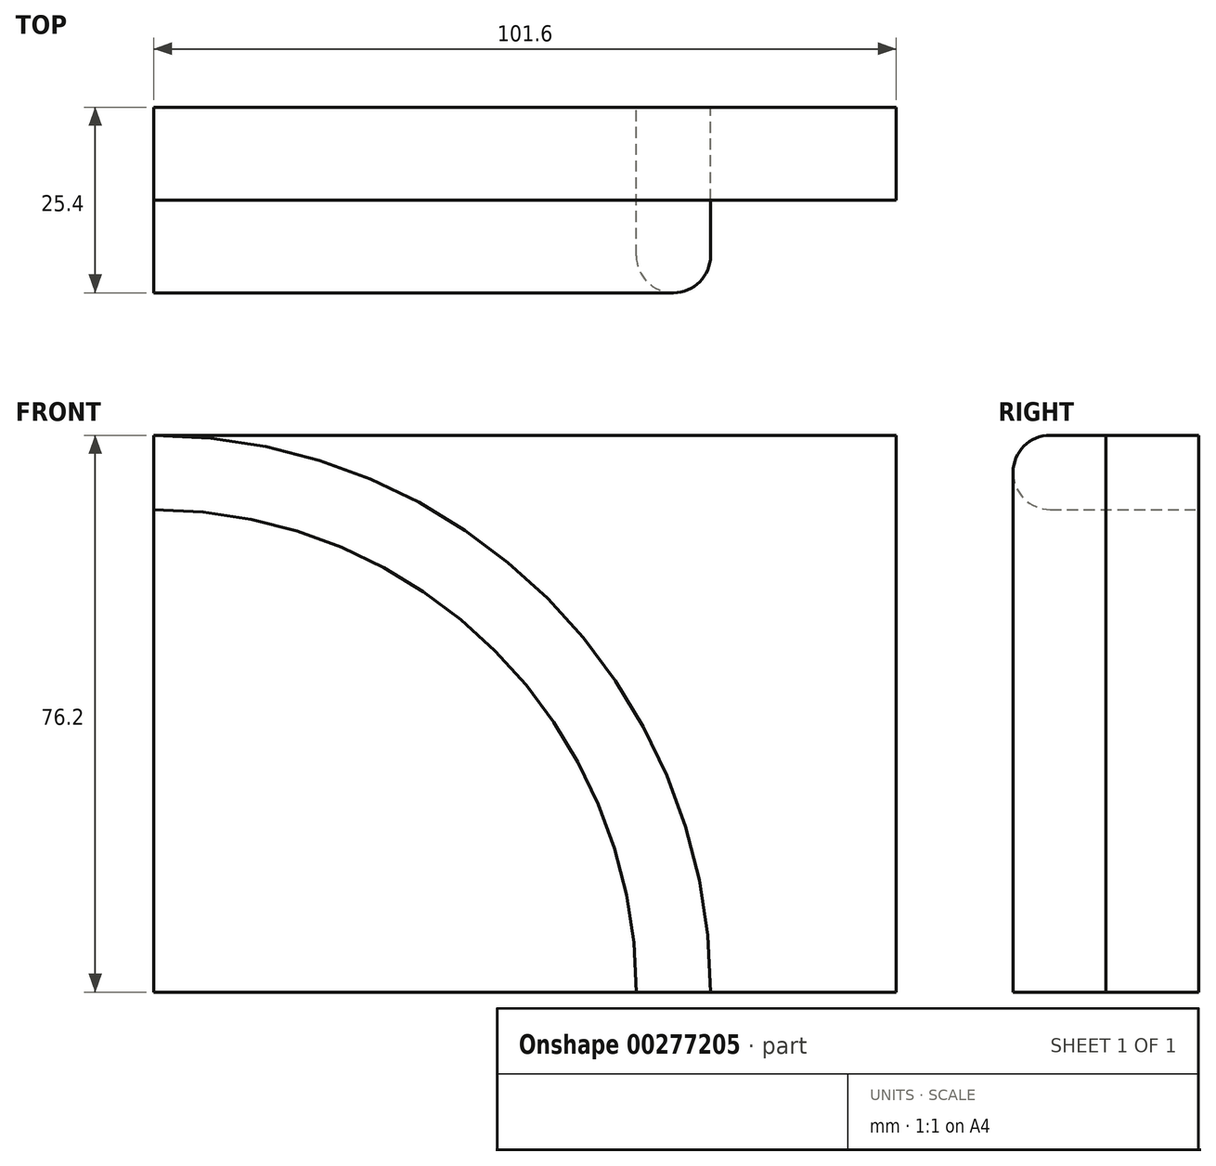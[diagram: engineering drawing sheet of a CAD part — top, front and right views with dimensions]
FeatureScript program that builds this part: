
annotation { "Feature Type Name" : "Feature", "Feature Type Description" : "" }
export const myFeature = defineFeature(function(context is Context, id is Id, definition is map)
    precondition{}
    {
        {
            var Q0;
            Q0=qCreatedBy(makeId("Front.planeOp"),FACE);
            var sketch = newSketch(context, id + "F0", { "sketchPlane" : qUnion([Q0])});
            skLineSegment(sketch, "E0.bottom", {"start": v(0, 0) * mm, "end": v(101.6, 0) * mm});
            skLineSegment(sketch, "E0.top", {"start": v(0, 76.2) * mm, "end": v(101.6, 76.2) * mm});
            skLineSegment(sketch, "E0.left", {"start": v(0, 0) * mm, "end": v(0, 76.2) * mm});
            skLineSegment(sketch, "E0.right", {"start": v(101.6, 0) * mm, "end": v(101.6, 76.2) * mm});
            skSolve(sketch);
        }
        {
            var Q0;
            Q0=makeQuery(id+"F0.imprint","IMPRINT",FACE,{"disambiguationData":[TD([[makeQuery(id+"F0.imprint","IMPRINT",EDGE,{"derivedFrom":sQuery(id+"F0.wireOp",EDGE,"E0.bottom")}),1.0]])]});
            extrude(context, id + "F1", {"entities" : qUnion([Q0]), "depth" : 12.7 * mm});
        }
        {
            var Q0;
            Q0=qCreatedBy(makeId("Front.planeOp"),FACE);
            var sketch = newSketch(context, id + "F2", { "sketchPlane" : qUnion([Q0])});
            skArc(sketch, "E1", {"start": v(0, 76.2) * mm, "mid": v(53.88, 53.88) * mm, "end": v(76.2, 0) * mm});
            skArc(sketch, "E2", {"start": v(0, 66.04) * mm, "mid": v(46.7, 46.7) * mm, "end": v(66.04, 0) * mm});
            skLineSegment(sketch, "E3", {"start": v(0, 76.2) * mm, "end": v(0, 66.04) * mm});
            skLineSegment(sketch, "E4", {"start": v(66.04, 0) * mm, "end": v(76.2, 0) * mm});
            skSolve(sketch);
        }
        {
            var Q0;
            Q0 = qSketchRegion(id + "F2", true);
            extrude(context, id + "F3", {"entities" : qUnion([Q0]), "depth" : 25.4 * mm});
        }
        {
            var Q0;
            Q0=makeQuery(id+"F3.opExtrude","CAP_EDGE",EDGE,{"disambiguationData":[OSD([sQuery(id+"F2.wireOp",EDGE,"E2")])],"isStart":false});
            var Q1;
            Q1=makeQuery(id+"F3.opExtrude","CAP_EDGE",EDGE,{"disambiguationData":[OSD([sQuery(id+"F2.wireOp",EDGE,"E1")])],"isStart":false});
            fillet(context, id + "F4", {"entities" : qUnion([Q0, Q1]), "radius" : 5.08 * mm, "tangentPropagation" : true, "allowEdgeOverflow" : false});
        }
    });
